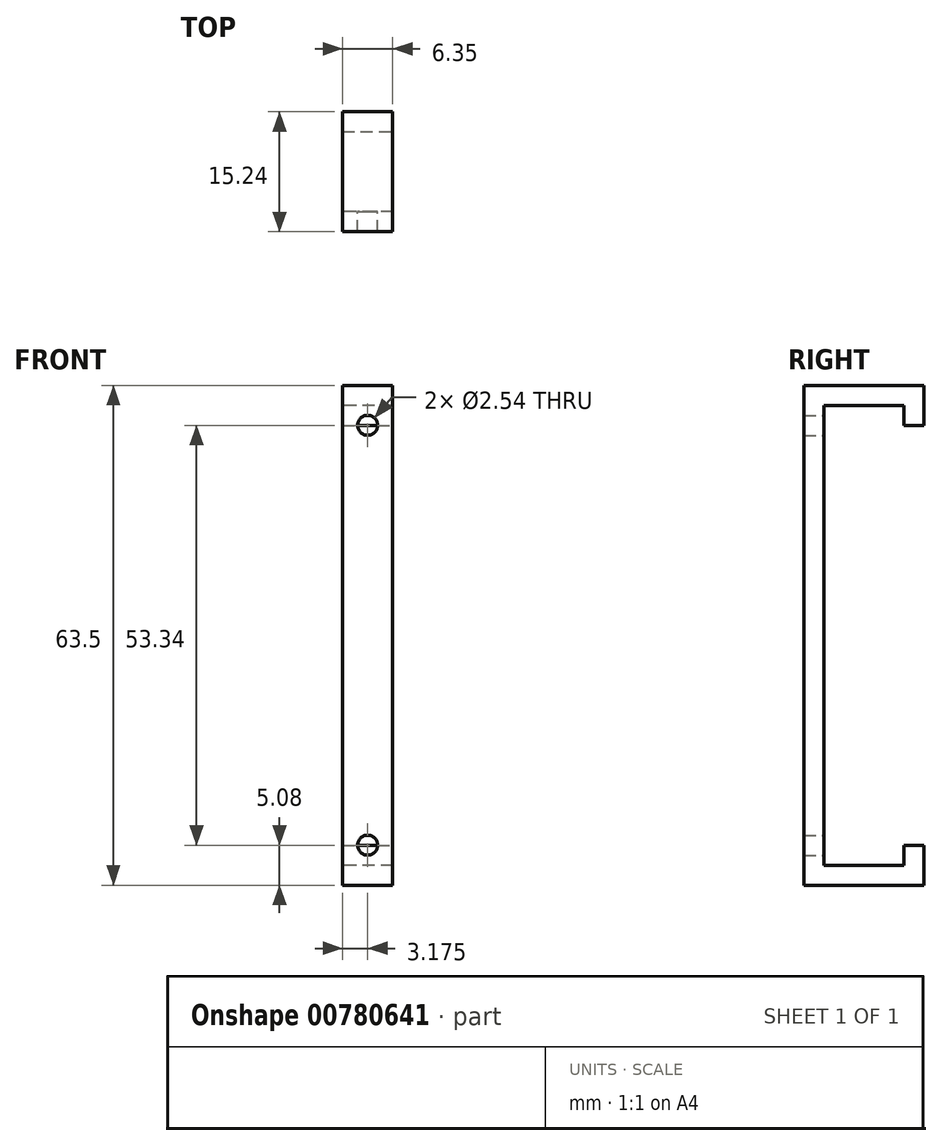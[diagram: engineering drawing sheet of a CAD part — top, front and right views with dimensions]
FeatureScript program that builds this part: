
annotation { "Feature Type Name" : "Feature", "Feature Type Description" : "" }
export const myFeature = defineFeature(function(context is Context, id is Id, definition is map)
    precondition{}
    {
        {
            var Q0;
            Q0=qCreatedBy(makeId("Top.planeOp"),FACE);
            var sketch = newSketch(context, id + "F0", { "sketchPlane" : qUnion([Q0])});
            skPoint(sketch, "E0.middle", {"position": v(0, 0) * mm});
            skLineSegment(sketch, "E1.bottom", {"start": v(-6.35, -15.24) * mm, "end": v(0, -15.24) * mm});
            skLineSegment(sketch, "E1.top", {"start": v(-6.35, 0) * mm, "end": v(0, 0) * mm});
            skLineSegment(sketch, "E1.left", {"start": v(-6.35, -15.24) * mm, "end": v(-6.35, 0) * mm});
            skLineSegment(sketch, "E1.right", {"start": v(0, -15.24) * mm, "end": v(0, 0) * mm});
            skSolve(sketch);
        }
        {
            var Q0;
            Q0 = qSketchRegion(id + "F0", true);
            extrude(context, id + "F1", {"entities" : qUnion([Q0]), "depth" : 63.5 * mm, "offsetDistance" : 25.4 * mm});
        }
        {
            var Q0;
            Q0=makeQuery(id+"F1.opExtrude","SWEPT_FACE",FACE,{"disambiguationData":[OSD([sQuery(id+"F0.wireOp",EDGE,"E1.left")])]});
            var sketch = newSketch(context, id + "F2", { "sketchPlane" : qUnion([Q0])});
            skLineSegment(sketch, "E2.bottom", {"start": v(2.54, 2.54) * mm, "end": v(12.7, 2.54) * mm});
            skLineSegment(sketch, "E2.top", {"start": v(2.54, 60.96) * mm, "end": v(12.7, 60.96) * mm});
            skLineSegment(sketch, "E2.left", {"start": v(2.54, 2.54) * mm, "end": v(2.54, 60.96) * mm});
            skLineSegment(sketch, "E2.right", {"start": v(12.7, 2.54) * mm, "end": v(12.7, 60.96) * mm});
            skSolve(sketch);
        }
        {
            var Q0;
            Q0 = qSketchRegion(id + "F2", true);
            extrude(context, id + "F3", {"entities" : qUnion([Q0]), "operationType" : NewBodyOperationType.REMOVE, "oppositeDirection" : true, "depth" : 25.4 * mm, "offsetDistance" : 25.4 * mm});
        }
        {
            var Q0;
            Q0=makeQuery(id+"F1.opExtrude","SWEPT_FACE",FACE,{"disambiguationData":[OSD([sQuery(id+"F0.wireOp",EDGE,"E1.left")])]});
            var sketch = newSketch(context, id + "F4", { "sketchPlane" : qUnion([Q0])});
            skLineSegment(sketch, "E3.bottom", {"start": v(-0.9, 5.08) * mm, "end": v(4.18, 5.08) * mm});
            skLineSegment(sketch, "E3.top", {"start": v(-0.9, 58.42) * mm, "end": v(4.18, 58.42) * mm});
            skLineSegment(sketch, "E3.left", {"start": v(-0.9, 5.08) * mm, "end": v(-0.9, 58.42) * mm});
            skLineSegment(sketch, "E3.right", {"start": v(4.18, 5.08) * mm, "end": v(4.18, 58.42) * mm});
            skSolve(sketch);
        }
        {
            var Q0;
            Q0 = qSketchRegion(id + "F4", true);
            extrude(context, id + "F5", {"entities" : qUnion([Q0]), "operationType" : NewBodyOperationType.REMOVE, "oppositeDirection" : true, "depth" : 25.4 * mm, "offsetDistance" : 25.4 * mm});
        }
        {
            var Q0;
            Q0=makeQuery(id+"F3.boolean.opBoolean","COPY",FACE,{"derivedFrom":makeQuery(id+"F3.opExtrude","SWEPT_FACE",FACE,{"disambiguationData":[OSD([sQuery(id+"F2.wireOp",EDGE,"E2.right")])]})});
            var sketch = newSketch(context, id + "F6", { "sketchPlane" : qUnion([Q0])});
            skCircle(sketch, "E4", {"center": v(3.18, 5.08) * mm, "radius": 1.27 * mm});
            skCircle(sketch, "E5", {"center": v(3.18, 58.42) * mm, "radius": 1.27 * mm});
            skSolve(sketch);
        }
        {
            var Q0;
            Q0 = qSketchRegion(id + "F6", true);
            extrude(context, id + "F7", {"entities" : qUnion([Q0]), "operationType" : NewBodyOperationType.REMOVE, "oppositeDirection" : true, "depth" : 25.4 * mm, "offsetDistance" : 25.4 * mm});
        }
    });
